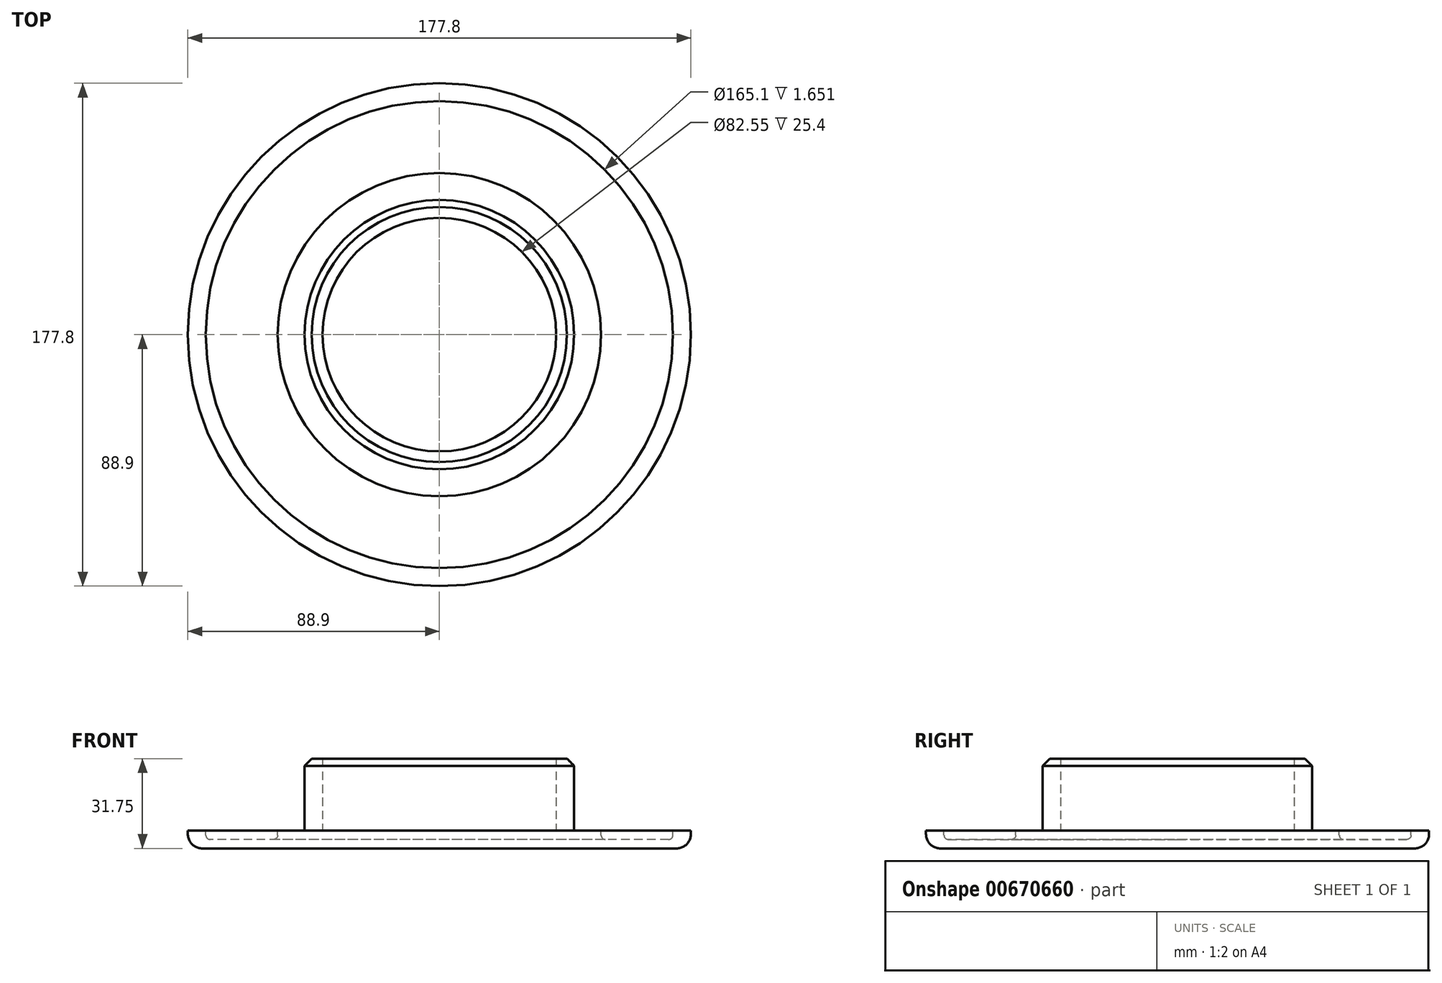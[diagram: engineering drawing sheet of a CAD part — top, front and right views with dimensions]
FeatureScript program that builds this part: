
annotation { "Feature Type Name" : "Feature", "Feature Type Description" : "" }
export const myFeature = defineFeature(function(context is Context, id is Id, definition is map)
    precondition{}
    {
        {
            var Q0;
            Q0=qCreatedBy(makeId("Top.planeOp"),FACE);
            var sketch = newSketch(context, id + "F0", { "sketchPlane" : qUnion([Q0])});
            skCircle(sketch, "E0", {"center": v(0, 0) * mm, "radius": 88.9 * mm});
            skSolve(sketch);
        }
        {
            var Q0;
            Q0=qCreatedBy(makeId("Top.planeOp"),FACE);
            var sketch = newSketch(context, id + "F1", { "sketchPlane" : qUnion([Q0])});
            skCircle(sketch, "E1", {"center": v(0, 0) * mm, "radius": 47.63 * mm});
            skSolve(sketch);
        }
        {
            var Q0;
            Q0 = qSketchRegion(id + "F1", true);
            extrude(context, id + "F2", {"entities" : qUnion([Q0]), "depth" : 25.4 * mm, "offsetDistance" : 25.4 * mm});
        }
        {
            var Q0;
            Q0=makeQuery(id+"F0.imprint","IMPRINT",FACE,{"disambiguationData":[TD([[makeQuery(id+"F0.imprint","IMPRINT",EDGE,{"derivedFrom":sQuery(id+"F0.wireOp",EDGE,"E0")}),1.0]])]});
            var Q1;
            Q1=makeQuery(id+"F2.opExtrude","CAP_FACE",FACE,{"disambiguationData":[OSD([sQuery(id+"F1.wireOp",EDGE,"E1")])],"isStart":false});
            extrude(context, id + "F3", {"entities" : qUnion([Q0, Q1]), "operationType" : NewBodyOperationType.ADD, "oppositeDirection" : true, "depth" : 6.35 * mm, "offsetDistance" : 25.4 * mm});
        }
        {
            var Q0;
            Q0=makeQuery(id+"F3.opExtrude","CAP_EDGE",EDGE,{"disambiguationData":[OSD([sQuery(id+"F0.wireOp",EDGE,"E0")])],"isStart":false});
            fillet(context, id + "F4", {"entities" : qUnion([Q0]), "radius" : 5.08 * mm, "tangentPropagation" : true, "allowEdgeOverflow" : false});
        }
        {
            var Q0;
            Q0=makeQuery(id+"F2.opExtrude","CAP_EDGE",EDGE,{"disambiguationData":[OSD([sQuery(id+"F1.wireOp",EDGE,"E1")])],"isStart":false});
            chamfer(context, id + "F5", {"entities" : qUnion([Q0]), "width" : 2.54 * mm, "tangentPropagation" : true});
        }
        {
            var Q0;
            Q0=qCreatedBy(makeId("Top.planeOp"),FACE);
            var sketch = newSketch(context, id + "F6", { "sketchPlane" : qUnion([Q0])});
            skCircle(sketch, "E2", {"center": v(0, 0) * mm, "radius": 57.15 * mm});
            skCircle(sketch, "E3", {"center": v(0, 0) * mm, "radius": 82.55 * mm});
            skSolve(sketch);
        }
        {
            var Q0;
            Q0=qCreatedBy(makeId("Top.planeOp"),FACE);
            var sketch = newSketch(context, id + "F7", { "sketchPlane" : qUnion([Q0])});
            skCircle(sketch, "E4", {"center": v(0, 0) * mm, "radius": 41.28 * mm});
            skSolve(sketch);
        }
        {
            var Q0;
            Q0 = qSketchRegion(id + "F6", true);
            extrude(context, id + "F8", {"entities" : qUnion([Q0]), "operationType" : NewBodyOperationType.REMOVE, "oppositeDirection" : true, "depth" : 3.17 * mm, "offsetDistance" : 25.4 * mm});
        }
        {
            var Q0;
            Q0 = qSketchRegion(id + "F7", true);
            extrude(context, id + "F9", {"entities" : qUnion([Q0]), "operationType" : NewBodyOperationType.REMOVE, "depth" : 25.4 * mm, "offsetDistance" : 25.4 * mm});
        }
        {
            var Q0;
            Q0=makeQuery(id+"F8.boolean.opBoolean","COPY",EDGE,{"derivedFrom":makeQuery(id+"F8.opExtrude","CAP_EDGE",EDGE,{"disambiguationData":[OSD([sQuery(id+"F6.wireOp",EDGE,"E3")])],"isStart":false})});
            var Q1;
            Q1=makeQuery(id+"F8.boolean.opBoolean","COPY",EDGE,{"derivedFrom":makeQuery(id+"F8.opExtrude","CAP_EDGE",EDGE,{"disambiguationData":[OSD([sQuery(id+"F6.wireOp",EDGE,"E2")])],"isStart":false})});
            var Q2;
            Q2=makeQuery(id+"F2.opExtrude","CAP_EDGE",EDGE,{"disambiguationData":[OSD([sQuery(id+"F1.wireOp",EDGE,"E1")])],"isStart":true});
            fillet(context, id + "F10", {"entities" : qUnion([Q0, Q1, Q2]), "radius" : 1.52 * mm, "tangentPropagation" : true, "allowEdgeOverflow" : false});
        }
    });
